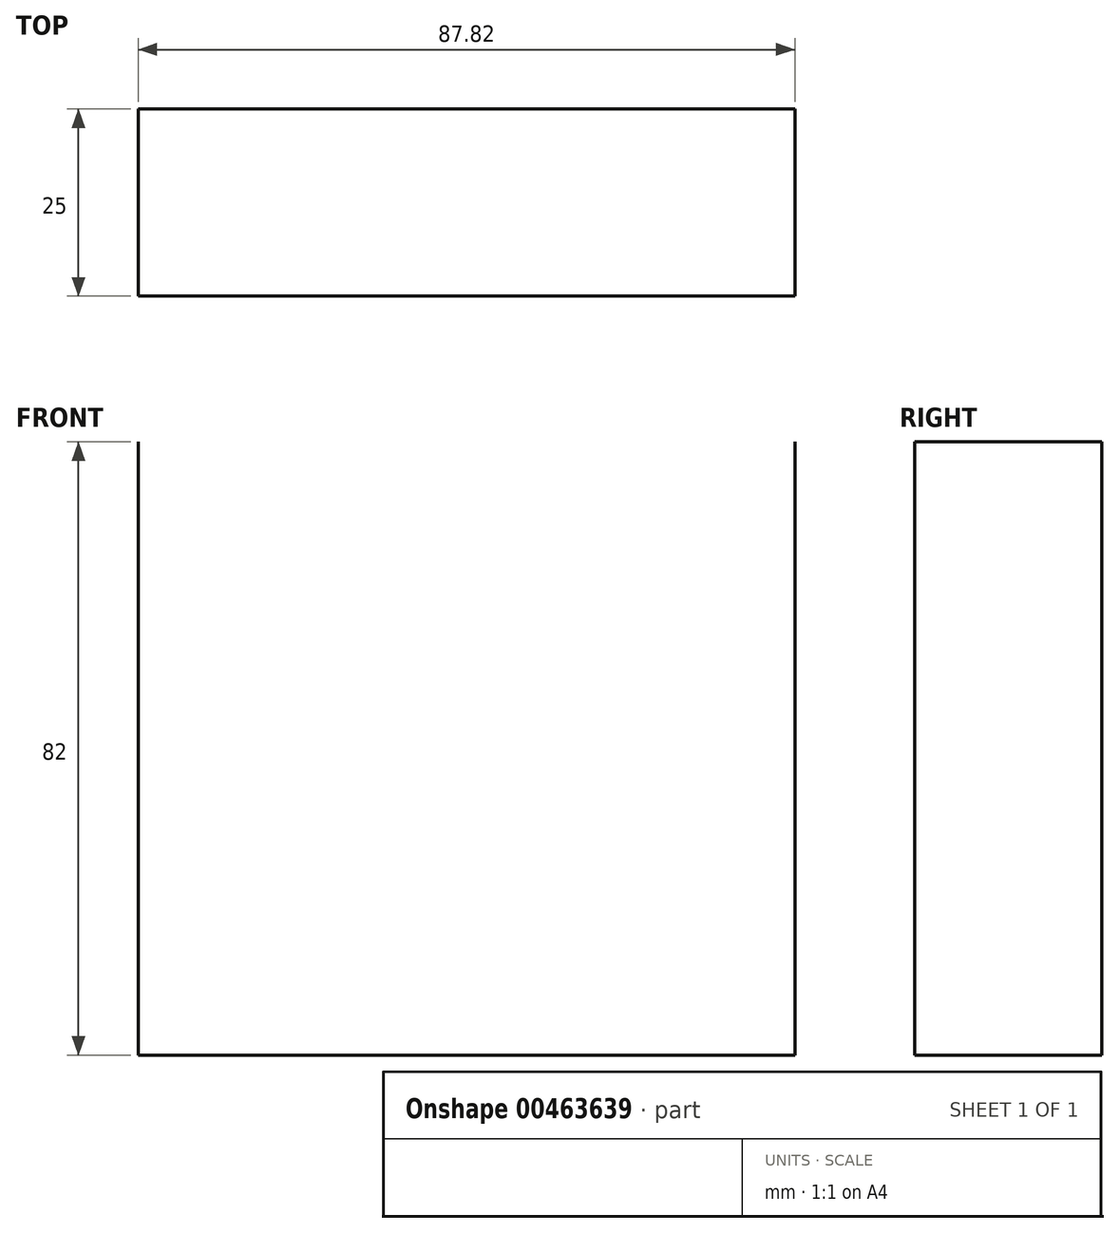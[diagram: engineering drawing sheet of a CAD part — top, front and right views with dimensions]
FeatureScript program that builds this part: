
annotation { "Feature Type Name" : "Feature", "Feature Type Description" : "" }
export const myFeature = defineFeature(function(context is Context, id is Id, definition is map)
    precondition{}
    {
        {
            var Q0;
            Q0=qCreatedBy(makeId("Front.planeOp"),FACE);
            var sketch = newSketch(context, id + "F0", { "sketchPlane" : qUnion([Q0])});
            skLineSegment(sketch, "E0.top", {"start": v(-32.28, -50.45) * mm, "end": v(55.54, -50.45) * mm});
            skLineSegment(sketch, "E0.left", {"start": v(-32.28, 31.55) * mm, "end": v(-32.28, -50.45) * mm});
            skLineSegment(sketch, "E0.right", {"start": v(55.54, 31.55) * mm, "end": v(55.54, -50.45) * mm});
            skSolve(sketch);
        }
        {
            var Q0;
            Q0 = qConstructionFilter(qBodyType(qCreatedBy(id + "F0" ,EDGE), BodyType.WIRE), ConstructionObject.NO);
            extrude(context, id + "F1", {"bodyType" : ToolBodyType.SURFACE, "surfaceEntities" : qUnion([Q0]), "depth" : 25 * mm});
        }
    });
